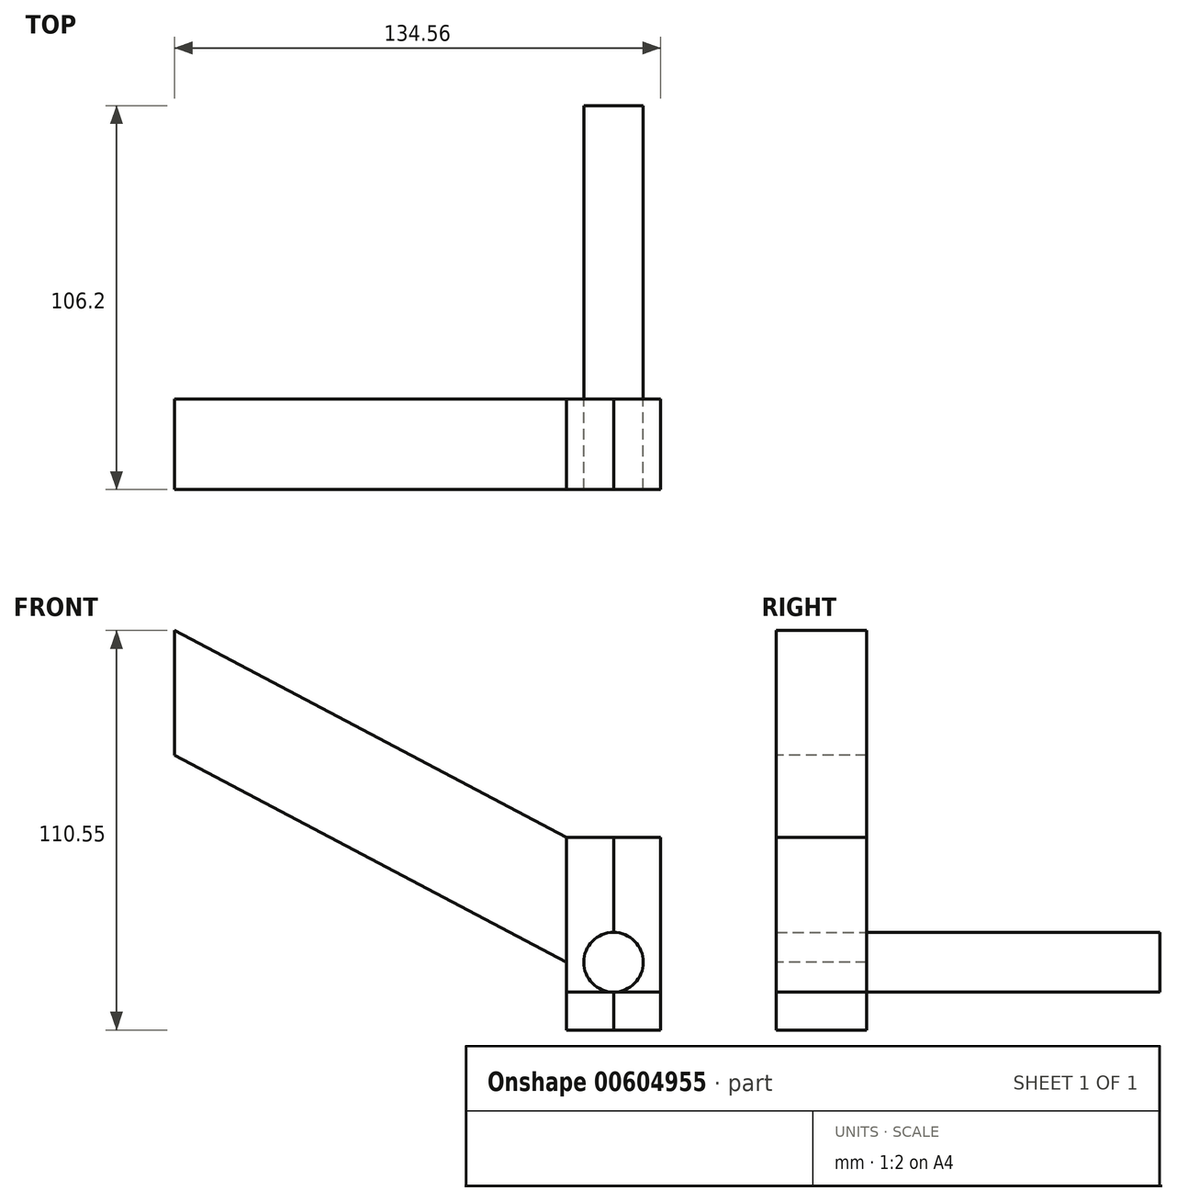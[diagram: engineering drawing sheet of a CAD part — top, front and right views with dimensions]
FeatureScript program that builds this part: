
annotation { "Feature Type Name" : "Feature", "Feature Type Description" : "" }
export const myFeature = defineFeature(function(context is Context, id is Id, definition is map)
    precondition{}
    {
        {
            var Q0;
            Q0=qCreatedBy(makeId("Front.planeOp"),FACE);
            var sketch = newSketch(context, id + "F0", { "sketchPlane" : qUnion([Q0])});
            skCircle(sketch, "E0", {"center": v(0, 0) * mm, "radius": 8.25 * mm});
            skSolve(sketch);
        }
        {
            var Q0;
            Q0=makeQuery(id+"F0.imprint","IMPRINT",FACE,{"disambiguationData":[TD([[makeQuery(id+"F0.imprint","IMPRINT",EDGE,{"derivedFrom":sQuery(id+"F0.wireOp",EDGE,"E0")}),1.0]])]});
            extrude(context, id + "F1", {"entities" : qUnion([Q0]), "depth" : 56.2 * mm, "offsetDistance" : 25 * mm});
        }
        {
            var Q0;
            Q0=makeQuery(id+"F1.opExtrude","CAP_FACE",FACE,{"disambiguationData":[OSD([sQuery(id+"F0.wireOp",EDGE,"E0")])],"isStart":false});
            var sketch = newSketch(context, id + "F2", { "sketchPlane" : qUnion([Q0])});
            skLineSegment(sketch, "E1.bottom", {"start": v(0, -8.25) * mm, "end": v(-13.03, -8.25) * mm});
            skLineSegment(sketch, "E1.top", {"start": v(0, 34.51) * mm, "end": v(-13.03, 34.51) * mm});
            skLineSegment(sketch, "E1.left", {"start": v(0, -8.25) * mm, "end": v(0, 34.51) * mm});
            skLineSegment(sketch, "E1.right", {"start": v(-13.03, -8.25) * mm, "end": v(-13.03, 34.51) * mm});
            skLineSegment(sketch, "E2.MirrorCS", {"start": v(13.03, -8.25) * mm, "end": v(13.03, 34.51) * mm});
            skLineSegment(sketch, "E3.MirrorCS", {"start": v(0, 34.51) * mm, "end": v(13.03, 34.51) * mm});
            skLineSegment(sketch, "E4.MirrorCS", {"start": v(0, -8.25) * mm, "end": v(13.03, -8.25) * mm});
            skSolve(sketch);
        }
        {
            var Q0;
            {var subQ4=sQuery(id+"F2.wireOp",EDGE,"E1.bottom");Q0=makeQuery(id+"F2.imprint","IMPRINT",FACE,{"disambiguationData":[TD([[makeQuery(id+"F2.imprint","IMPRINT",EDGE,{"derivedFrom":subQ4}),-1.0]])]});}
            extrude(context, id + "F3", {"entities" : qUnion([Q0]), "depth" : 25 * mm, "offsetDistance" : 25 * mm});
        }
        {
            var Q0;
            Q0=makeQuery(id+"F2.imprint","IMPRINT",FACE,{"disambiguationData":[TD([[makeQuery(id+"F2.imprint","IMPRINT",EDGE,{"derivedFrom":sQuery(id+"F2.wireOp",EDGE,"E2.MirrorCS")}),1.0]])]});
            extrude(context, id + "F4", {"entities" : qUnion([Q0]), "depth" : 25 * mm, "offsetDistance" : 25 * mm});
        }
        {
            var Q0;
            Q0=makeQuery(id+"F3.opExtrude","CAP_FACE",FACE,{"disambiguationData":[OSD([sQuery(id+"F0.wireOp",EDGE,"E0"),sQuery(id+"F2.wireOp",EDGE,"E1.bottom"),sQuery(id+"F2.wireOp",EDGE,"E1.top"),sQuery(id+"F2.wireOp",EDGE,"E1.left"),sQuery(id+"F2.wireOp",EDGE,"E1.right")])],"isStart":false});
            var sketch = newSketch(context, id + "F5", { "sketchPlane" : qUnion([Q0])});
            skLineSegment(sketch, "E5", {"start": v(-13.03, 34.51) * mm, "end": v(-121.53, 91.8) * mm});
            skLineSegment(sketch, "E6", {"start": v(-121.53, 91.8) * mm, "end": v(-121.53, 57.29) * mm});
            skLineSegment(sketch, "E7", {"start": v(-121.53, 57.29) * mm, "end": v(-13.03, 0) * mm});
            skLineSegment(sketch, "E8", {"start": v(-13.03, 34.51) * mm, "end": v(-13.03, 0) * mm});
            skSolve(sketch);
        }
        {
            var Q0;
            Q0=makeQuery(id+"F5.imprint","IMPRINT",FACE,{"disambiguationData":[TD([[makeQuery(id+"F5.imprint","IMPRINT",EDGE,{"derivedFrom":sQuery(id+"F5.wireOp",EDGE,"E5")}),1.0]])]});
            extrude(context, id + "F6", {"entities" : qUnion([Q0]), "oppositeDirection" : true, "depth" : 25 * mm, "offsetDistance" : 25 * mm});
        }
        {
            var Q0;
            Q0=makeQuery(id+"F3.opExtrude","SWEPT_FACE",FACE,{"disambiguationData":[OSD([sQuery(id+"F2.wireOp",EDGE,"E1.bottom")])]});
            var Q1;
            Q1=makeQuery(id+"F4.opExtrude","SWEPT_FACE",FACE,{"disambiguationData":[OSD([sQuery(id+"F2.wireOp",EDGE,"E4.MirrorCS")])]});
            extrude(context, id + "F7", {"entities" : qUnion([Q0, Q1]), "depth" : 10.5 * mm, "offsetDistance" : 25 * mm});
        }
        {
            var Q0;
            Q0=makeQuery(id+"F1.opExtrude","CAP_FACE",FACE,{"disambiguationData":[OSD([sQuery(id+"F0.wireOp",EDGE,"E0")])],"isStart":false});
            extrude(context, id + "F8", {"entities" : qUnion([Q0]), "depth" : 25 * mm, "offsetDistance" : 25 * mm});
        }
        {
            var Q0;
            Q0=makeQuery(id+"F1.opExtrude","CAP_FACE",FACE,{"disambiguationData":[OSD([sQuery(id+"F0.wireOp",EDGE,"E0")])],"isStart":true});
            extrude(context, id + "F9", {"entities" : qUnion([Q0]), "operationType" : NewBodyOperationType.ADD, "depth" : 25 * mm, "offsetDistance" : 25 * mm});
        }
    });
